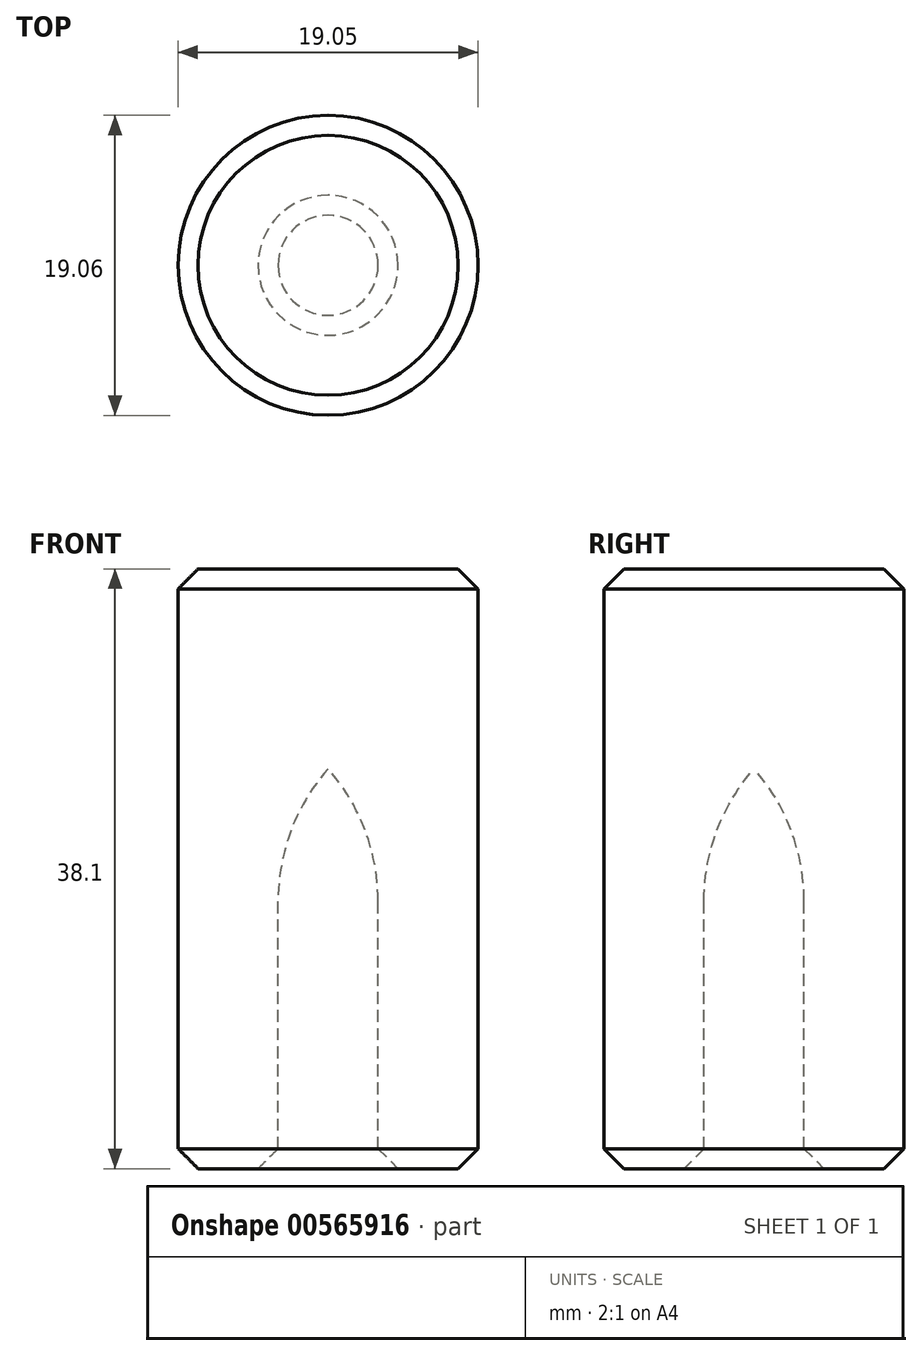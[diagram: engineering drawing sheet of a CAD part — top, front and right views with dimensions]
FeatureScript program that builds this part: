
annotation { "Feature Type Name" : "Feature", "Feature Type Description" : "" }
export const myFeature = defineFeature(function(context is Context, id is Id, definition is map)
    precondition{}
    {
        {
            var Q0;
            Q0=qCreatedBy(makeId("Front.planeOp"),FACE);
            var sketch = newSketch(context, id + "F0", { "sketchPlane" : qUnion([Q0])});
            skLineSegment(sketch, "E0", {"start": v(0, 0) * mm, "end": v(0, 36.83) * mm});
            skLineSegment(sketch, "E1", {"start": v(9.53, 38.1) * mm, "end": v(9.53, 25.4) * mm});
            skLineSegment(sketch, "E2", {"start": v(0, 0) * mm, "end": v(6.35, 0) * mm});
            skLineSegment(sketch, "E3", {"start": v(6.35, 0) * mm, "end": v(6.35, 17) * mm});
            skArc(sketch, "E4", {"start": v(9.52, 25.4) * mm, "mid": v(7.17, 21.49) * mm, "end": v(6.35, 17) * mm});
            skArc(sketch, "E5", {"start": v(9.52, 38.1) * mm, "mid": v(4.72, 37.78) * mm, "end": v(0, 36.83) * mm});
            skPoint(sketch, "E6.orphan", {"position": v(0, 38.1) * mm});
            skLineSegment(sketch, "E7", {"start": v(9.52, 38.1) * mm, "end": v(20.84, 38.1) * mm, "construction": true});
            skLineSegment(sketch, "E8", {"start": v(0, 36.83) * mm, "end": v(0, 38.1) * mm});
            skLineSegment(sketch, "E9", {"start": v(0, 38.1) * mm, "end": v(9.53, 38.1) * mm});
            skSolve(sketch);
        }
        {
            var Q0;
            Q0 = qSketchRegion(id + "F0", true);
            var Q1;
            Q1=sQuery(id+"F0.wireOp",EDGE,"E1");
            revolve(context, id + "F1", {"entities" : qUnion([Q0]), "axis" : qUnion([Q1]), "revolveType" : RevolveType.FULL});
        }
        {
            var Q0;
            Q0=makeQuery(id+"F1.opRevolve","SWEPT_FACE",FACE,{"disambiguationData":[OSD([sQuery(id+"F0.wireOp",EDGE,"E0"),sQuery(id+"F0.wireOp",EDGE,"E8")])]});
            var Q1;
            Q1=makeQuery(id+"F1.opRevolve","SWEPT_FACE",FACE,{"disambiguationData":[OSD([sQuery(id+"F0.wireOp",EDGE,"E2")])]});
            chamfer(context, id + "F2", {"entities" : qUnion([Q0, Q1]), "width" : 1.27 * mm, "tangentPropagation" : true});
        }
    });
